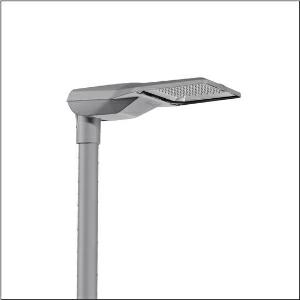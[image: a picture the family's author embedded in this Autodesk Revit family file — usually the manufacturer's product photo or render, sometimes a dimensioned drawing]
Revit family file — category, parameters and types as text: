
# Revit family: streetlight_sl_21_iq_midi___pl52_5xe3h41d08mb_c975
name_source: partatom
category: Lighting Fixtures
units: mm (PartAtom-declared; Revit-internal decimal feet)

## family parameters
Cut with Voids When Loaded = No
Host = Face
Light Source = No
Part Type = Normal
Room Calculation Point = No
Round Connector Dimension = Use Diameter
Shared = No

## types (1)
- --- (1 x LED, 20000 lm, 146.7 W, 4000K)
    Apparent Load = 147 VA
    CIE Flux Codes = 27 59 98 100 100
    Color Rendering = 70
    Color Temperature = 4000K
    Default Elevation = 1800 mm
    Description = Streetlight SL 21 iQ midi, mast luminaire, primary light control with lens, of PMMA, primary optical cover: cover, of toughened safety glass, transparent, light distribution: PL52, light emission: direct distribution, primary light characteristic: asymmetric, installation type: post-top, side-entry, LED, High Power LED, rated luminous flux: 20.000lm, luminous efficacy: 136lm/W, light colour: 740, colour temperature: 4000K, control: Auto-Match, Temp-Guard, Lumen-Switch, Night-Set, Smart-Wire, Light-Fading, Desk-Remote (wireless, voltage-free reading and setting of iQ features in the workshop via application-optimized NFC function/RFID function), optimised constant luminous flux control (CLO 2.0), presetting dimming linear, mains connection: 230..240V, AC, 50/60Hz, start of lifetime: 147W, end of service life: 161W, reduction: 62W, luminaire housing, of diecast aluminium, powder-coated, Siteco® metallic grey (DB 702S), corrosivity category C5 mid according to DIN EN ISO 12944, please order mast flange separately, inclination adjustable: 0°, 5°, 10°, 15°, sealing non-destructively replaceable, multi-level sealing system, length: 644mm, width: 335mm, height: 110mm, mast flange for spigot size: 42mm (side-entry): 5XC10008XM4, 60/48mm (side-entry/post-top): 5XC10108XM2, 76/60mm (side-entry/post-top): 5XC10108XM1, protection rating (complete): IP66, insulation class (complete): insulation class II (safety insulation), certification: CE, ENEC, ENEC+, VDE, impact resistance: IK09, permissible operating ambient temperature for outdoor applications: -40..+50°C, standard-compliant lighting for roads and squares, packaging unit: 1 piece

Light Distribution: PL52
    Height = 111 mm
    Lamp = 1 x LED
    Lamp Light Flux = 20000 lm
    Lamp Power = 146.7 W
    Lamp count = 1
    Length = 644 mm
    Luminous efficacy = 136 lm/W
    Manufacturer = Siteco
    ModVariant = No
    Model = 5XE3H41D08MB
    Number of Poles = 1
    OnlyDefault = Yes
    Power Factor = 1
    Product Name = Streetlight SL 21 iQ midi | PL52
    Product group = mast luminaire | pylon top
    ProductGroupID = 6100
    Protection Class = Protection class II
    Protection Degree = IP 66
    RLX_Detail_Level = 1
    RLX_Emergency_Light_Flux = 0 lm
    RLX_Emergency_Type = 0
    RLX_Emergency_Type_DB = No
    RlxData = <blob elided: 100093 chars, md5=a0bcfa1e>
    Socket = socket
    Standby Power = 0 W
    System Light Flux = 20000 lm
    System Power = 147 W
    Type Comments = factory setting: luminous flux: 100 % | dim-lin: 254 | 753 mA
    Type Image = l_1004298.jpg
    URL = http://relux.com
    VarID = @adj_143217
    Voltage = 0 V
    Weight = 0.00 kg
    Width = 336 mm

## geometry (parser evidence)
native form markers: Blend x4, Sweep x8
no freeform markers — native parametric forms only
